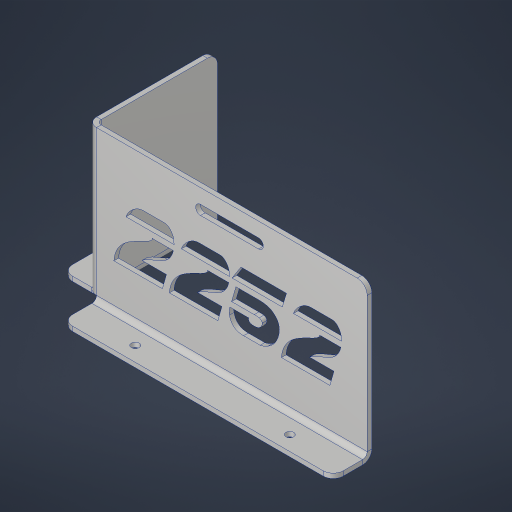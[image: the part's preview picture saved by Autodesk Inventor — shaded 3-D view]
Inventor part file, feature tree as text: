
AUTODESK INVENTOR PART (.ipt)
format: ipt  version: 2023.4 (Build 274418000, 418)  size: 376,320 bytes
history: native  units: in
note: dims shown in document units (in); Inventor stores cm internally (conversion verified against a paired STEP export)
features: sheet_metal_op x7, sketch x6, other x4, emboss x1, hole x1, fillet x1
ambient origin geometry x8: Origin, YZ Plane, XZ Plane, XY Plane, X Axis, Y Axis, Z Axis, Center Point
bodies: Solid1 (feature_tree)
feature tree (20):
  sheet_metal_op  "Face1"
  sheet_metal_op  "Flange1"
  sheet_metal_op  "Flange2"
  emboss  "Emboss1"
  hole  "Hole1"  [1 undecoded]
  fillet  "Fillet1"  Radius=0.12in
  sketch  "Sketch1"  dims[d0=7.125in d1=4.0in d2=0.12in]
  other  "Plate1"
  sketch  "Sketch2"  dims[d3=0.12in]
  other  "Plate2"
  sheet_metal_op  "Bend1"
  sheet_metal_op  "Corner1"
  sketch  "Sketch3"  dims[d4=0.06in]
  other  "Plate3"
  sheet_metal_op  "Bend2"
  sheet_metal_op  "Corner2"
  sketch  "Sketch4"  dims[d5=0.24in]
  sketch  "Sketch5"  dims[d6=0.12in]
  sketch  "Sketch6"  dims[d7=3.25in d8=90.0deg d9=0.12in d10=0.48in d11=0.12in d12=0.12in d13=0.12in d14=0.06in d15=0.24in d16=0.12in d17=1.0in d18=90.0deg d19=0.12in d20=0.48in d21=0.12in d22=0.12in d24=0.25in d25=1.5in d26=0.5in d27=0.12in d28=0.0in d29=0.25in d30=0.0in d31=1.5in d32=4.0in d33=0.201in d34=0.38in d35=0.385in d36=0.25in d37=0.5635in d38=0.12in d39=0.8108in d40=0.26in]
  other  "Cut1"
note: 1 required parameter value undecoded (feature->parameter linkage not recoverable at this tier; creation-order binding heuristic only, values carry confidence <= 0.55)
